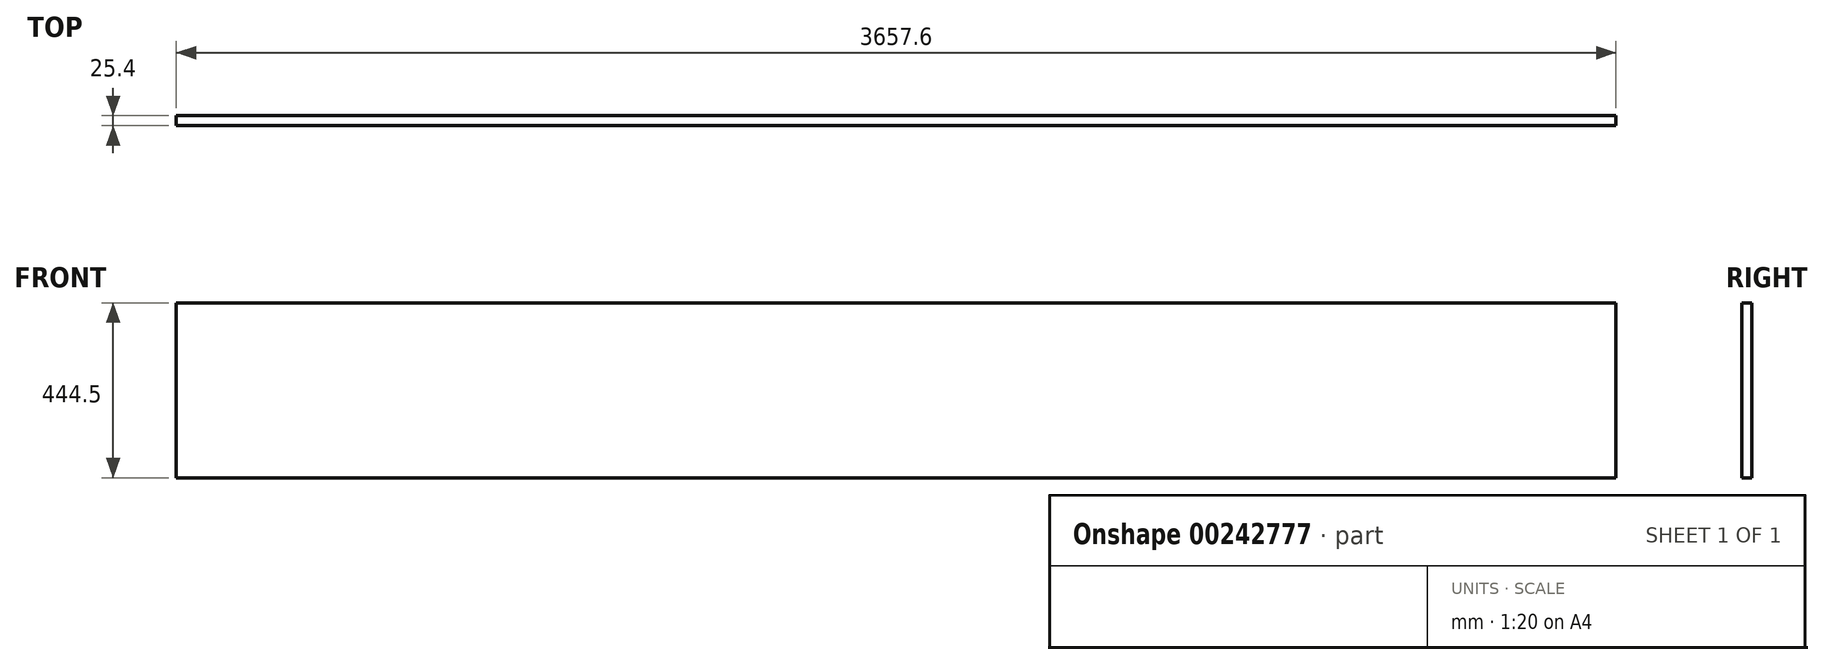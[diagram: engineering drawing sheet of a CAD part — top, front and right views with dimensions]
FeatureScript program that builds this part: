
annotation { "Feature Type Name" : "Feature", "Feature Type Description" : "" }
export const myFeature = defineFeature(function(context is Context, id is Id, definition is map)
    precondition{}
    {
        {
            var Q0;
            Q0=qCreatedBy(makeId("Front.planeOp"),FACE);
            var sketch = newSketch(context, id + "F0", { "sketchPlane" : qUnion([Q0])});
            skLineSegment(sketch, "E0.bottom", {"start": v(0, 0) * mm, "end": v(3657.6, 0) * mm});
            skLineSegment(sketch, "E0.top", {"start": v(0, 444.5) * mm, "end": v(3657.6, 444.5) * mm});
            skLineSegment(sketch, "E0.left", {"start": v(0, 0) * mm, "end": v(0, 444.5) * mm});
            skLineSegment(sketch, "E0.right", {"start": v(3657.6, 0) * mm, "end": v(3657.6, 444.5) * mm});
            skSolve(sketch);
        }
        {
            var Q0;
            Q0=makeQuery(id+"F0.imprint","IMPRINT",FACE,{"disambiguationData":[TD([[makeQuery(id+"F0.imprint","IMPRINT",EDGE,{"derivedFrom":sQuery(id+"F0.wireOp",EDGE,"E0.bottom")}),1.0]])]});
            extrude(context, id + "F1", {"entities" : qUnion([Q0]), "depth" : 25.4 * mm});
        }
    });
